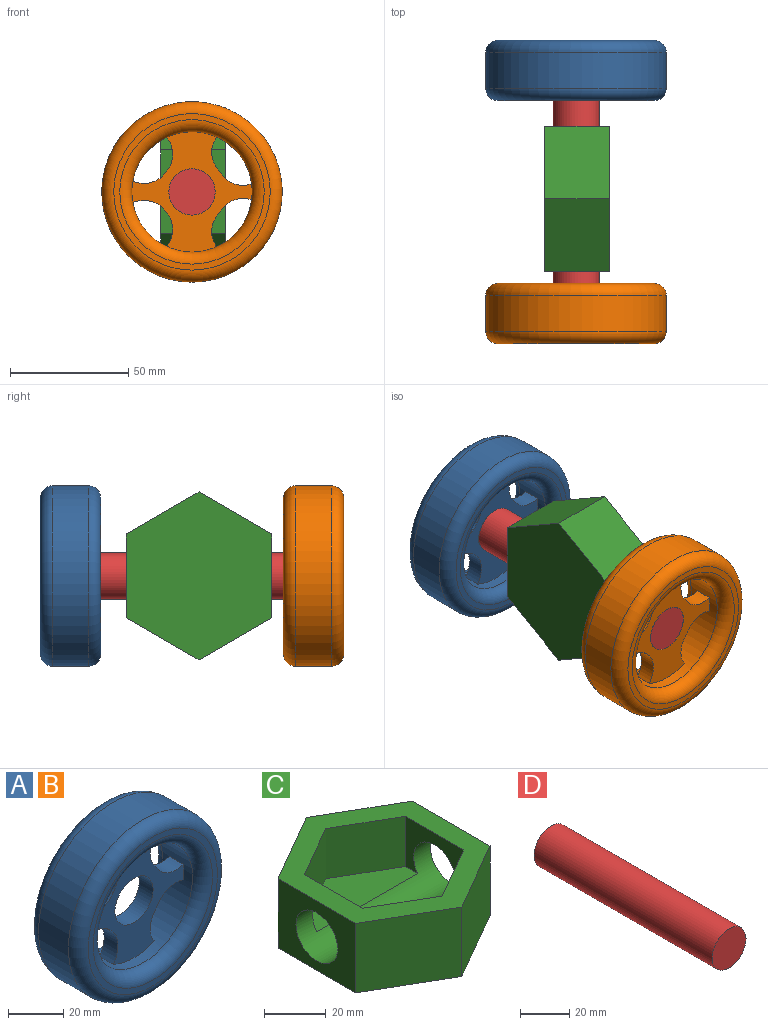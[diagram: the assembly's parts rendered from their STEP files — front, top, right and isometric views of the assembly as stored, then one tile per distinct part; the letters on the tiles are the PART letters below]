
ASSEMBLY  parts=4 mates=5
PART A: 19 faces, bbox 82.5x25.4x82.5 mm
  f0: cylinder r=25.4mm len=50.8mm, axis (0,1,0), area 2008.8mm2, adj f4,f6,f8,f9,f10,f11,f12,f13
  f1: cylinder r=38.1mm len=76.2mm, axis (0,1,0), area 3648.3mm2, adj f5,f7
  f2: plane 66.04x66.04mm, normal (0,-1,0), area 506.7mm2, adj f6,f7
  f3: plane 66.04x66.04mm, normal (0,1,0), area 506.7mm2, adj f4,f5
  f4: torus R=30.48mm, axis (0,-1,0), area 1366mm2, adj f0,f3
  f5: torus R=33.02mm, axis (0,-1,0), area 1817.7mm2, adj f1,f3
  f6: torus R=30.48mm, axis (0,-1,0), area 1366mm2, adj f0,f2
  f7: torus R=33.02mm, axis (0,-1,0), area 1817.7mm2, adj f1,f2
  f8: cylinder r=11.65mm len=14.35mm, axis (0,1,0), area 109.9mm2, adj f0,f16,f17,f18
  f9: cylinder r=10.88mm len=14.43mm, axis (0,1,0), area 112.8mm2, adj f0,f10,f17,f18
  f10: cylinder r=10.87mm len=13.44mm, axis (0,1,0), area 112.3mm2, adj f0,f9,f17,f18
  f11: cylinder r=10.87mm len=13.44mm, axis (0,1,0), area 112.3mm2, adj f0,f12,f17,f18
  f12: cylinder r=10.88mm len=14.43mm, axis (0,1,0), area 112.8mm2, adj f0,f11,f17,f18
  f13: cylinder r=11.65mm len=14.35mm, axis (0,1,0), area 109.9mm2, adj f0,f14,f17,f18
  f14: cylinder r=11.68mm len=14.36mm, axis (0,1,0), area 115.4mm2, adj f0,f13,f17,f18
  f15: cylinder r=9.78mm len=19.56mm, axis (0,1,0), area 437mm2, adj f17,f18
  f16: cylinder r=11.68mm len=14.36mm, axis (0,1,0), area 115.4mm2, adj f0,f8,f17,f18
  f17: plane 50.8x50.8mm, normal (0,-1,0), area 924.4mm2, adj f0,f8,f9,f10,f11,f12,f13,f14
  f18: plane 50.8x50.8mm, normal (0,1,0), area 924.4mm2, adj f0,f8,f9,f10,f11,f12,f13,f14
PART B: same geometry as A
PART C: 17 faces, bbox 61.4x70.9x27.4 mm
  f0: plane 46.12x18.98mm, normal (0,0,1), area 568.2mm2, adj f12,f13,f14,f15,f16
  f1: plane 46.12x18.98mm, normal (0,0,1), area 568.2mm2, adj f10,f11,f12,f15,f16
  f2: plane 70.85x61.36mm, normal (0,0,1), area 1418.6mm2, adj f3,f4,f5,f6,f7,f8,f10,f11
  f3: plane 30.68x27.43mm, normal (0.5,0.87,0), area 971.8mm2, adj f2,f4,f8,f9
  f4: plane 30.68x27.43mm, normal (-0.5,0.87,0), area 971.8mm2, adj f2,f3,f5,f9
  f5: plane 35.43x27.43mm, normal (-1,0,0), area 686.8mm2, adj f2,f4,f6,f9,f16
  f6: plane 30.68x27.43mm, normal (-0.5,-0.87,0), area 971.8mm2, adj f2,f5,f7,f9
  f7: plane 30.68x27.43mm, normal (0.5,-0.87,0), area 971.8mm2, adj f2,f6,f8,f9
  f8: plane 35.43x27.43mm, normal (1,0,0), area 686.8mm2, adj f2,f3,f7,f9,f16
  f9: plane 70.85x61.36mm, normal (0,0,-1), area 3260.7mm2, adj f3,f4,f5,f6,f7,f8
  f10: plane 23.06x19.81mm, normal (-0.5,-0.87,0), area 527.6mm2, adj f1,f2,f11,f15
  f11: plane 23.06x19.81mm, normal (0.5,-0.87,0), area 527.6mm2, adj f1,f2,f10,f12
  f12: plane 26.63x19.81mm, normal (1,0,0), area 283.8mm2, adj f0,f1,f2,f11,f13,f16
  f13: plane 23.06x19.81mm, normal (0.5,0.87,0), area 527.6mm2, adj f0,f2,f12,f14
  f14: plane 23.06x19.81mm, normal (-0.5,0.87,0), area 527.6mm2, adj f0,f2,f13,f15
  f15: plane 26.63x19.81mm, normal (-1,0,0), area 283.8mm2, adj f0,f1,f2,f10,f14,f16
  f16: cylinder r=9.53mm len=61.36mm, axis (1,0,0), area 1731.7mm2, adj f0,f1,f5,f8,f12,f15
PART D: 3 faces, bbox 19.6x102.6x19.6 mm
  f0: cylinder r=9.78mm len=102.62mm, axis (0,1,0), area 6305.1mm2, adj f1,f2
  f1: plane 19.56x19.56mm, normal (0,-1,0), area 300.4mm2, adj f0
  f2: plane 19.56x19.56mm, normal (0,1,0), area 300.4mm2, adj f0
PLACE A t=(-85.77,-1.35,-41.33)mm
PLACE B t=(-85.77,-103.97,-41.33)mm
PLACE C rot(axis=(0.58,0.58,0.58),120deg) t=(-71.63,-37.64,-41.33)mm
PLACE D t=(-85.77,-17.01,-41.33)mm
MATE cylindrical C.f16 <-> D.f0  axis (0,1,0) through (-85.77,-68.32,-41.33)mm
MATE slider D.f0 <-> A.f0  axis (0,1,0) through (-85.77,-17.01,-41.33)mm
MATE slider D.f0 <-> B.f0  axis (0,-1,0) through (-85.77,-119.63,-41.33)mm
MATE slider B.f0 <-> D.f0  axis (0,1,0) through (-85.77,-116.16,-41.33)mm
MATE pin_slot C.f16 <-> D.f0  axis (0,1,0) through (-85.77,-68.32,-41.33)mm
